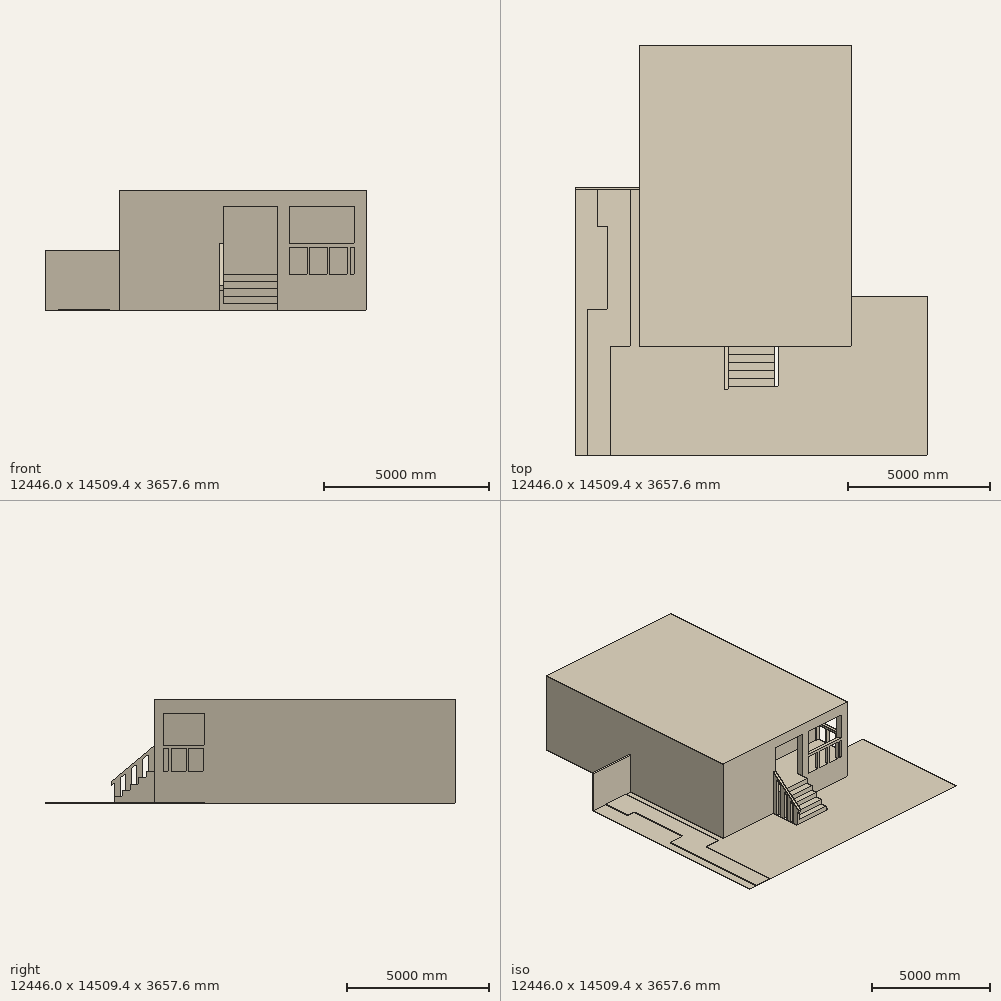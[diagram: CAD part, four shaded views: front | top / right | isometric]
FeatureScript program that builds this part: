
annotation { "Feature Type Name" : "Feature", "Feature Type Description" : "" }
export const myFeature = defineFeature(function(context is Context, id is Id, definition is map)
    precondition{}
    {
        {
            var Q0;
            Q0=qCreatedBy(makeId("Top.planeOp"),FACE);
            var sketch = newSketch(context, id + "F0", { "sketchPlane" : qUnion([Q0])});
            skLineSegment(sketch, "E0", {"start": v(0, 0) * mm, "end": v(0, 5562.6) * mm});
            skLineSegment(sketch, "E1", {"start": v(0, 5562.6) * mm, "end": v(-558.8, 5562.6) * mm});
            skLineSegment(sketch, "E2", {"start": v(-558.8, 5562.6) * mm, "end": v(-1498.6, 5562.6) * mm});
            skLineSegment(sketch, "E3", {"start": v(-1498.6, 5562.6) * mm, "end": v(-2260.6, 5562.6) * mm});
            skLineSegment(sketch, "E4", {"start": v(-2260.6, 5562.6) * mm, "end": v(-2260.6, -3860.8) * mm});
            skLineSegment(sketch, "E5", {"start": v(-2260.6, -3860.8) * mm, "end": v(10185.4, -3860.8) * mm});
            skLineSegment(sketch, "E6", {"start": v(10185.4, -3860.8) * mm, "end": v(10185.4, 0) * mm});
            skLineSegment(sketch, "E7", {"start": v(10185.4, 0) * mm, "end": v(10185.4, 2841.96) * mm});
            skLineSegment(sketch, "E8", {"start": v(10185.4, 2841.96) * mm, "end": v(10185.4, 6391.8) * mm});
            skLineSegment(sketch, "E9", {"start": v(10185.4, 6391.8) * mm, "end": v(7493, 6391.8) * mm});
            skLineSegment(sketch, "E10", {"start": v(7493, 6391.8) * mm, "end": v(7493, 1778) * mm});
            skLineSegment(sketch, "E11", {"start": v(7493, 1778) * mm, "end": v(7493, 0) * mm});
            skLineSegment(sketch, "E12", {"start": v(7493, 0) * mm, "end": v(4775.2, 0) * mm});
            skLineSegment(sketch, "E13", {"start": v(4775.2, 0) * mm, "end": v(4775.2, -1422.4) * mm});
            skLineSegment(sketch, "E14", {"start": v(4775.2, -1422.4) * mm, "end": v(4775.2, -3860.8) * mm});
            skLineSegment(sketch, "E15", {"start": v(0, 0) * mm, "end": v(3149.6, 0) * mm});
            skLineSegment(sketch, "E16", {"start": v(3149.6, 0) * mm, "end": v(3149.6, -1422.4) * mm});
            skLineSegment(sketch, "E17", {"start": v(3149.6, -1422.4) * mm, "end": v(2895.6, -1422.4) * mm});
            skLineSegment(sketch, "E18", {"start": v(2895.6, -1422.4) * mm, "end": v(2895.6, -3860.8) * mm});
            skLineSegment(sketch, "E19", {"start": v(-2134.8, -5689.6) * mm, "end": v(10320.05, -5689.6) * mm});
            skLineSegment(sketch, "E20", {"start": v(-2158.89, -6502.4) * mm, "end": v(10392.32, -6502.4) * mm});
            skSolve(sketch);
        }
        {
            var Q0;
            Q0=qCreatedBy(makeId("Top.planeOp"),FACE);
            var sketch = newSketch(context, id + "F1", { "sketchPlane" : qUnion([Q0])});
            skLineSegment(sketch, "E21.bottom", {"start": v(-1498.6, 5562.6) * mm, "end": v(-304.8, 5562.6) * mm});
            skLineSegment(sketch, "E22.left", {"start": v(-1117.6, 4241.8) * mm, "end": v(-1117.6, 1320.8) * mm});
            skLineSegment(sketch, "E22.right", {"start": v(-304.8, 4244.88) * mm, "end": v(-304.8, 0) * mm});
            skLineSegment(sketch, "E23.bottom", {"start": v(-1854.2, 1320.8) * mm, "end": v(-1117.6, 1320.8) * mm});
            skLineSegment(sketch, "E23.top", {"start": v(-1854.2, -3860.8) * mm, "end": v(-1041.4, -3860.8) * mm});
            skLineSegment(sketch, "E23.left", {"start": v(-1854.2, 1320.8) * mm, "end": v(-1854.2, -3860.8) * mm});
            skLineSegment(sketch, "E23.right", {"start": v(-1041.4, 0) * mm, "end": v(-1041.4, -3860.8) * mm});
            skLineSegment(sketch, "E24.top", {"start": v(-304.8, 0) * mm, "end": v(-1041.4, 0) * mm});
            skLineSegment(sketch, "E24.left", {"start": v(-304.8, 0) * mm, "end": v(-304.8, 0) * mm});
            skLineSegment(sketch, "E25", {"start": v(-304.8, 4244.88) * mm, "end": v(-304.8, 5562.6) * mm});
            skLineSegment(sketch, "E26", {"start": v(-1117.6, 4241.8) * mm, "end": v(-1498.6, 4241.8) * mm});
            skLineSegment(sketch, "E27", {"start": v(-1498.6, 4241.8) * mm, "end": v(-1498.6, 5562.6) * mm});
            skSolve(sketch);
        }
        {
            var Q0;
            Q0=qCreatedBy(makeId("Top.planeOp"),FACE);
            var sketch = newSketch(context, id + "F2", { "sketchPlane" : qUnion([Q0])});
            skLineSegment(sketch, "E28.bottom", {"start": v(0, 0) * mm, "end": v(7493, 0) * mm});
            skLineSegment(sketch, "E28.top", {"start": v(0, 10648.55) * mm, "end": v(7493, 10648.55) * mm});
            skLineSegment(sketch, "E28.left", {"start": v(0, 0) * mm, "end": v(0, 10648.55) * mm});
            skLineSegment(sketch, "E28.right", {"start": v(7493, 0) * mm, "end": v(7493, 10648.55) * mm});
            skSolve(sketch);
        }
        {
            var Q0;
            Q0 = qSketchRegion(id + "F2", true);
            extrude(context, id + "F3", {"entities" : qUnion([Q0]), "depth" : 3657.6 * mm, "offsetDistance" : 25.4 * mm});
        }
        {
            var Q0;
            Q0=makeQuery(id+"F3.opExtrude","SWEPT_FACE",FACE,{"disambiguationData":[OSD([sQuery(id+"F2.wireOp",EDGE,"E28.bottom")])]});
            var sketch = newSketch(context, id + "F4", { "sketchPlane" : qUnion([Q0])});
            skLineSegment(sketch, "E29.bottom", {"start": v(7493, 3167.33) * mm, "end": v(3149.6, 3167.33) * mm});
            skLineSegment(sketch, "E29.top", {"start": v(7493, 1114.2) * mm, "end": v(3149.6, 1114.2) * mm});
            skLineSegment(sketch, "E29.left", {"start": v(7493, 3167.33) * mm, "end": v(7493, 1114.2) * mm});
            skLineSegment(sketch, "E29.right", {"start": v(3149.6, 3167.33) * mm, "end": v(3149.6, 1114.2) * mm});
            skSolve(sketch);
        }
        {
            var Q0;
            Q0 = qSketchRegion(id + "F4", true);
            extrude(context, id + "F5", {"entities" : qUnion([Q0]), "operationType" : NewBodyOperationType.REMOVE, "oppositeDirection" : true, "depth" : 1778 * mm, "offsetDistance" : 25.4 * mm});
        }
        {
            var Q0;
            Q0=makeQuery(id+"F5.boolean.opBoolean","COPY",FACE,{"derivedFrom":makeQuery(id+"F5.opExtrude","SWEPT_FACE",FACE,{"disambiguationData":[OSD([sQuery(id+"F4.wireOp",EDGE,"E29.top")])]})});
            var sketch = newSketch(context, id + "F6", { "sketchPlane" : qUnion([Q0])});
            skLineSegment(sketch, "E30", {"start": v(4775.2, 0) * mm, "end": v(4775.2, 152.4) * mm});
            skLineSegment(sketch, "E31", {"start": v(4775.2, 152.4) * mm, "end": v(7340.6, 152.4) * mm});
            skLineSegment(sketch, "E32", {"start": v(7340.6, 152.4) * mm, "end": v(7340.6, 1778) * mm});
            skLineSegment(sketch, "E33", {"start": v(7340.6, 1778) * mm, "end": v(7493, 1778) * mm});
            skLineSegment(sketch, "E34", {"start": v(7493, 1778) * mm, "end": v(7493, 0) * mm});
            skLineSegment(sketch, "E35", {"start": v(7493, 0) * mm, "end": v(4775.2, 0) * mm});
            skSolve(sketch);
        }
        {
            var Q0;
            Q0=makeQuery(id+"F6.imprint","IMPRINT",FACE,{"disambiguationData":[TD([[makeQuery(id+"F6.imprint","IMPRINT",EDGE,{"derivedFrom":sQuery(id+"F6.wireOp",EDGE,"E30")}),-1.0]])]});
            extrude(context, id + "F7", {"entities" : qUnion([Q0]), "operationType" : NewBodyOperationType.ADD, "depth" : 914.4 * mm, "offsetDistance" : 25.4 * mm});
        }
        {
            var Q0;
            Q0=makeQuery(id+"F7.boolean.opBoolean","MERGE",FACE,{"derivedFrom":[makeQuery(id+"F3.opExtrude","SWEPT_FACE",FACE,{"disambiguationData":[OSD([sQuery(id+"F2.wireOp",EDGE,"E28.bottom")])]}),makeQuery(id+"F7.opExtrude","SWEPT_FACE",FACE,{"disambiguationData":[OSD([sQuery(id+"F6.wireOp",EDGE,"E35")])]})]});
            var sketch = newSketch(context, id + "F8", { "sketchPlane" : qUnion([Q0])});
            skLineSegment(sketch, "E36.bottom", {"start": v(5080, 1927) * mm, "end": v(5156.2, 1927) * mm, "construction": true});
            skLineSegment(sketch, "E36.top", {"start": v(5080, 1114.2) * mm, "end": v(5156.2, 1114.2) * mm, "construction": true});
            skLineSegment(sketch, "E36.left", {"start": v(5080, 1927) * mm, "end": v(5080, 1114.2) * mm, "construction": true});
            skLineSegment(sketch, "E36.right", {"start": v(5156.2, 1927) * mm, "end": v(5156.2, 1114.2) * mm, "construction": true});
            skLineSegment(sketch, "E37.1.0.0", {"start": v(5765.8, 1927) * mm, "end": v(5765.8, 1114.2) * mm, "construction": true});
            skLineSegment(sketch, "E37.1.0.1", {"start": v(5689.6, 1927) * mm, "end": v(5765.8, 1927) * mm, "construction": true});
            skLineSegment(sketch, "E37.1.0.2", {"start": v(5689.6, 1927) * mm, "end": v(5689.6, 1114.2) * mm, "construction": true});
            skLineSegment(sketch, "E37.1.0.3", {"start": v(5689.6, 1114.2) * mm, "end": v(5765.8, 1114.2) * mm, "construction": true});
            skLineSegment(sketch, "E37.2.0.0", {"start": v(6375.4, 1927) * mm, "end": v(6375.4, 1114.2) * mm, "construction": true});
            skLineSegment(sketch, "E37.2.0.1", {"start": v(6299.2, 1927) * mm, "end": v(6375.4, 1927) * mm, "construction": true});
            skLineSegment(sketch, "E37.2.0.2", {"start": v(6299.2, 1927) * mm, "end": v(6299.2, 1114.2) * mm, "construction": true});
            skLineSegment(sketch, "E37.2.0.3", {"start": v(6299.2, 1114.2) * mm, "end": v(6375.4, 1114.2) * mm, "construction": true});
            skLineSegment(sketch, "E37.3.0.0", {"start": v(6985, 1927) * mm, "end": v(6985, 1114.2) * mm, "construction": true});
            skLineSegment(sketch, "E37.3.0.1", {"start": v(6908.8, 1927) * mm, "end": v(6985, 1927) * mm, "construction": true});
            skLineSegment(sketch, "E37.3.0.2", {"start": v(6908.8, 1927) * mm, "end": v(6908.8, 1114.2) * mm, "construction": true});
            skLineSegment(sketch, "E37.3.0.3", {"start": v(6908.8, 1114.2) * mm, "end": v(6985, 1114.2) * mm, "construction": true});
            skLineSegment(sketch, "E37.direction1", {"start": v(5156.2, 1114.2) * mm, "end": v(5765.8, 1114.2) * mm, "construction": true});
            skLineSegment(sketch, "E38.bottom", {"start": v(5156.2, 1927) * mm, "end": v(5689.6, 1927) * mm, "construction": true});
            skLineSegment(sketch, "E38.top", {"start": v(5156.2, 1114.2) * mm, "end": v(5689.6, 1114.2) * mm, "construction": true});
            skLineSegment(sketch, "E39.bottom", {"start": v(5765.8, 1114.2) * mm, "end": v(6299.2, 1114.2) * mm, "construction": true});
            skLineSegment(sketch, "E39.top", {"start": v(5765.8, 1927) * mm, "end": v(6299.2, 1927) * mm, "construction": true});
            skLineSegment(sketch, "E39.left", {"start": v(5765.8, 1114.2) * mm, "end": v(5765.8, 1927) * mm, "construction": true});
            skLineSegment(sketch, "E39.right", {"start": v(6299.2, 1114.2) * mm, "end": v(6299.2, 1927) * mm, "construction": true});
            skLineSegment(sketch, "E40.bottom", {"start": v(6375.4, 1927) * mm, "end": v(6908.8, 1927) * mm, "construction": true});
            skLineSegment(sketch, "E40.top", {"start": v(6375.4, 1114.2) * mm, "end": v(6908.8, 1114.2) * mm, "construction": true});
            skLineSegment(sketch, "E41.bottom", {"start": v(5156.2, 1927) * mm, "end": v(5689.6, 1927) * mm});
            skLineSegment(sketch, "E41.top", {"start": v(5156.2, 1114.2) * mm, "end": v(5689.6, 1114.2) * mm});
            skLineSegment(sketch, "E41.left", {"start": v(5156.2, 1927) * mm, "end": v(5156.2, 1114.2) * mm});
            skLineSegment(sketch, "E41.right", {"start": v(5689.6, 1927) * mm, "end": v(5689.6, 1114.2) * mm});
            skLineSegment(sketch, "E42.bottom", {"start": v(5765.8, 1114.2) * mm, "end": v(6299.2, 1114.2) * mm});
            skLineSegment(sketch, "E42.top", {"start": v(5765.8, 1927) * mm, "end": v(6299.2, 1927) * mm});
            skLineSegment(sketch, "E42.left", {"start": v(5765.8, 1114.2) * mm, "end": v(5765.8, 1927) * mm});
            skLineSegment(sketch, "E42.right", {"start": v(6299.2, 1114.2) * mm, "end": v(6299.2, 1927) * mm});
            skLineSegment(sketch, "E43.bottom", {"start": v(6375.4, 1927) * mm, "end": v(6908.8, 1927) * mm});
            skLineSegment(sketch, "E43.top", {"start": v(6375.4, 1114.2) * mm, "end": v(6908.8, 1114.2) * mm});
            skLineSegment(sketch, "E43.left", {"start": v(6375.4, 1927) * mm, "end": v(6375.4, 1114.2) * mm});
            skLineSegment(sketch, "E43.right", {"start": v(6908.8, 1927) * mm, "end": v(6908.8, 1114.2) * mm});
            skSolve(sketch);
        }
        {
            var Q0;
            Q0 = qSketchRegion(id + "F8", true);
            extrude(context, id + "F9", {"entities" : qUnion([Q0]), "operationType" : NewBodyOperationType.REMOVE, "oppositeDirection" : true, "depth" : 304.8 * mm, "offsetDistance" : 25.4 * mm});
        }
        {
            var Q0;
            Q0=makeQuery(id+"F7.boolean.opBoolean","MERGE",FACE,{"derivedFrom":[makeQuery(id+"F3.opExtrude","SWEPT_FACE",FACE,{"disambiguationData":[OSD([sQuery(id+"F2.wireOp",EDGE,"E28.right")])]}),makeQuery(id+"F7.opExtrude","SWEPT_FACE",FACE,{"disambiguationData":[OSD([sQuery(id+"F6.wireOp",EDGE,"E34")])]})]});
            var sketch = newSketch(context, id + "F10", { "sketchPlane" : qUnion([Q0])});
            skLineSegment(sketch, "E44.bottom", {"start": v(1727.2, 1927) * mm, "end": v(1193.8, 1927) * mm});
            skLineSegment(sketch, "E44.top", {"start": v(1727.2, 1114.2) * mm, "end": v(1193.8, 1114.2) * mm});
            skLineSegment(sketch, "E44.left", {"start": v(1727.2, 1927) * mm, "end": v(1727.2, 1114.2) * mm});
            skLineSegment(sketch, "E44.right", {"start": v(1193.8, 1927) * mm, "end": v(1193.8, 1114.2) * mm});
            skLineSegment(sketch, "E45.bottom", {"start": v(1117.6, 1927) * mm, "end": v(584.2, 1927) * mm});
            skLineSegment(sketch, "E45.top", {"start": v(1117.6, 1114.2) * mm, "end": v(584.2, 1114.2) * mm});
            skLineSegment(sketch, "E45.left", {"start": v(1117.6, 1927) * mm, "end": v(1117.6, 1114.2) * mm});
            skLineSegment(sketch, "E45.right", {"start": v(584.2, 1927) * mm, "end": v(584.2, 1114.2) * mm});
            skSolve(sketch);
        }
        {
            var Q0;
            Q0 = qSketchRegion(id + "F10", true);
            extrude(context, id + "F11", {"entities" : qUnion([Q0]), "operationType" : NewBodyOperationType.REMOVE, "oppositeDirection" : true, "depth" : 254 * mm, "offsetDistance" : 25.4 * mm});
        }
        {
            var Q0;
            Q0=makeQuery(id+"F11.boolean.opBoolean","MERGE",FACE,{"derivedFrom":[makeQuery(id+"F9.boolean.opBoolean","MERGE",FACE,{"derivedFrom":[makeQuery(id+"F5.boolean.opBoolean","COPY",FACE,{"derivedFrom":makeQuery(id+"F5.opExtrude","SWEPT_FACE",FACE,{"disambiguationData":[OSD([sQuery(id+"F4.wireOp",EDGE,"E29.top")])]})}),makeQuery(id+"F9.opExtrude","SWEPT_FACE",FACE,{"disambiguationData":[OSD([sQuery(id+"F8.wireOp",EDGE,"E41.top")])]}),makeQuery(id+"F9.opExtrude","SWEPT_FACE",FACE,{"disambiguationData":[OSD([sQuery(id+"F8.wireOp",EDGE,"E42.bottom")])]}),makeQuery(id+"F9.opExtrude","SWEPT_FACE",FACE,{"disambiguationData":[OSD([sQuery(id+"F8.wireOp",EDGE,"E43.top")])]})]}),makeQuery(id+"F11.opExtrude","SWEPT_FACE",FACE,{"disambiguationData":[OSD([sQuery(id+"F10.wireOp",EDGE,"E44.top")])]}),makeQuery(id+"F11.opExtrude","SWEPT_FACE",FACE,{"disambiguationData":[OSD([sQuery(id+"F10.wireOp",EDGE,"E45.top")])]})]});
            var sketch = newSketch(context, id + "F12", { "sketchPlane" : qUnion([Q0])});
            skLineSegment(sketch, "E46.bottom", {"start": v(4775.2, 0) * mm, "end": v(5156.2, 0) * mm});
            skLineSegment(sketch, "E46.top", {"start": v(4775.2, 304.8) * mm, "end": v(5156.2, 304.8) * mm});
            skLineSegment(sketch, "E46.left", {"start": v(4775.2, 0) * mm, "end": v(4775.2, 304.8) * mm});
            skLineSegment(sketch, "E46.right", {"start": v(5156.2, 0) * mm, "end": v(5156.2, 304.8) * mm});
            skLineSegment(sketch, "E47.bottom", {"start": v(7112, 304.8) * mm, "end": v(7493, 304.8) * mm});
            skLineSegment(sketch, "E47.top", {"start": v(7112, 0) * mm, "end": v(7493, 0) * mm});
            skLineSegment(sketch, "E47.left", {"start": v(7112, 304.8) * mm, "end": v(7112, 0) * mm});
            skLineSegment(sketch, "E47.right", {"start": v(7493, 304.8) * mm, "end": v(7493, 0) * mm});
            skSolve(sketch);
        }
        {
            var Q0;
            Q0 = qSketchRegion(id + "F12", true);
            extrude(context, id + "F13", {"entities" : qUnion([Q0]), "operationType" : NewBodyOperationType.ADD, "depth" : 2540 * mm, "offsetDistance" : 25.4 * mm});
        }
        {
            var Q0;
            Q0=makeQuery(id+"F13.boolean.opBoolean","MERGE",FACE,{"derivedFrom":[makeQuery(id+"F7.boolean.opBoolean","MERGE",FACE,{"derivedFrom":[makeQuery(id+"F3.opExtrude","SWEPT_FACE",FACE,{"disambiguationData":[OSD([sQuery(id+"F2.wireOp",EDGE,"E28.right")])]}),makeQuery(id+"F7.opExtrude","SWEPT_FACE",FACE,{"disambiguationData":[OSD([sQuery(id+"F6.wireOp",EDGE,"E34")])]})]}),makeQuery(id+"F13.opExtrude","SWEPT_FACE",FACE,{"disambiguationData":[OSD([sQuery(id+"F12.wireOp",EDGE,"E47.right")])]})]});
            var sketch = newSketch(context, id + "F14", { "sketchPlane" : qUnion([Q0])});
            skLineSegment(sketch, "E48.bottom", {"start": v(508, 1927) * mm, "end": v(304.8, 1927) * mm});
            skLineSegment(sketch, "E48.top", {"start": v(508, 1114.2) * mm, "end": v(304.8, 1114.2) * mm});
            skLineSegment(sketch, "E48.left", {"start": v(508, 1927) * mm, "end": v(508, 1114.2) * mm});
            skLineSegment(sketch, "E48.right", {"start": v(304.8, 1927) * mm, "end": v(304.8, 1114.2) * mm});
            skSolve(sketch);
        }
        {
            var Q0;
            Q0 = qSketchRegion(id + "F14", true);
            extrude(context, id + "F15", {"entities" : qUnion([Q0]), "operationType" : NewBodyOperationType.REMOVE, "oppositeDirection" : true, "depth" : 254 * mm, "offsetDistance" : 25.4 * mm});
        }
        {
            var Q0;
            Q0=makeQuery(id+"F13.boolean.opBoolean","MERGE",FACE,{"derivedFrom":[makeQuery(id+"F7.boolean.opBoolean","MERGE",FACE,{"derivedFrom":[makeQuery(id+"F3.opExtrude","SWEPT_FACE",FACE,{"disambiguationData":[OSD([sQuery(id+"F2.wireOp",EDGE,"E28.bottom")])]}),makeQuery(id+"F7.opExtrude","SWEPT_FACE",FACE,{"disambiguationData":[OSD([sQuery(id+"F6.wireOp",EDGE,"E35")])]})]}),makeQuery(id+"F13.opExtrude","SWEPT_FACE",FACE,{"disambiguationData":[OSD([sQuery(id+"F12.wireOp",EDGE,"E46.bottom")])]}),makeQuery(id+"F13.opExtrude","SWEPT_FACE",FACE,{"disambiguationData":[OSD([sQuery(id+"F12.wireOp",EDGE,"E47.top")])]})]});
            var sketch = newSketch(context, id + "F16", { "sketchPlane" : qUnion([Q0])});
            skLineSegment(sketch, "E49.bottom", {"start": v(6985, 1927) * mm, "end": v(7112, 1927) * mm});
            skLineSegment(sketch, "E49.top", {"start": v(6985, 1114.2) * mm, "end": v(7112, 1114.2) * mm});
            skLineSegment(sketch, "E49.left", {"start": v(6985, 1927) * mm, "end": v(6985, 1114.2) * mm});
            skLineSegment(sketch, "E49.right", {"start": v(7112, 1927) * mm, "end": v(7112, 1114.2) * mm});
            skSolve(sketch);
        }
        {
            var Q0;
            Q0=makeQuery(id+"F5.boolean.opBoolean","COPY",FACE,{"derivedFrom":makeQuery(id+"F5.opExtrude","SWEPT_FACE",FACE,{"disambiguationData":[OSD([sQuery(id+"F4.wireOp",EDGE,"E29.right")])]})});
            cPlane(context, id + "F17", {"entities" : qUnion([Q0]), "cplaneType" : CPlaneType.OFFSET, "offset" : 0 * mm, "width" : 152.4 * mm, "height" : 152.4 * mm});
        }
        {
            var Q0;
            Q0 = qSketchRegion(id + "F16", true);
            extrude(context, id + "F18", {"entities" : qUnion([Q0]), "operationType" : NewBodyOperationType.REMOVE, "oppositeDirection" : true, "depth" : 254 * mm, "offsetDistance" : 25.4 * mm});
        }
        {
            var Q0;
            Q0=qCreatedBy(id+"F17.planeOp",FACE);
            var sketch = newSketch(context, id + "F19", { "sketchPlane" : qUnion([Q0])});
            skLineSegment(sketch, "E50", {"start": v(0, 1114.2) * mm, "end": v(-284.48, 1114.2) * mm});
            skLineSegment(sketch, "E51", {"start": v(-284.48, 891.36) * mm, "end": v(-568.96, 891.36) * mm});
            skLineSegment(sketch, "E52", {"start": v(-568.96, 891.36) * mm, "end": v(-568.96, 668.52) * mm});
            skLineSegment(sketch, "E53", {"start": v(-568.96, 668.52) * mm, "end": v(-853.44, 668.52) * mm});
            skLineSegment(sketch, "E54", {"start": v(-853.44, 668.52) * mm, "end": v(-853.44, 445.68) * mm});
            skLineSegment(sketch, "E55", {"start": v(-1422.4, 222.84) * mm, "end": v(-1422.4, 0) * mm});
            skLineSegment(sketch, "E56", {"start": v(-1422.4, 0) * mm, "end": v(0, 0) * mm});
            skLineSegment(sketch, "E57", {"start": v(0, 0) * mm, "end": v(0, 1114.2) * mm});
            skLineSegment(sketch, "E58", {"start": v(-1422.4, 222.84) * mm, "end": v(-1137.92, 222.84) * mm});
            skLineSegment(sketch, "E59", {"start": v(-1137.92, 222.84) * mm, "end": v(-1137.92, 445.68) * mm});
            skLineSegment(sketch, "E60", {"start": v(-1137.92, 445.68) * mm, "end": v(-853.44, 445.68) * mm});
            skLineSegment(sketch, "E61", {"start": v(-284.48, 891.36) * mm, "end": v(-284.48, 1114.2) * mm});
            skSolve(sketch);
        }
        {
            var Q0;
            Q0 = qSketchRegion(id + "F19", true);
            var Q1;
            Q1=makeQuery(id+"F13.boolean.opBoolean","MERGE",FACE,{"derivedFrom":[makeQuery(id+"F7.opExtrude","SWEPT_FACE",FACE,{"disambiguationData":[OSD([sQuery(id+"F6.wireOp",EDGE,"E30")])]}),makeQuery(id+"F13.opExtrude","SWEPT_FACE",FACE,{"disambiguationData":[OSD([sQuery(id+"F12.wireOp",EDGE,"E46.left")])]})]});
            extrude(context, id + "F20", {"entities" : qUnion([Q0]), "operationType" : NewBodyOperationType.ADD, "endBound" : BoundingType.UP_TO_SURFACE, "depth" : 25.4 * mm, "endBoundEntityFace" : qUnion([Q1]), "offsetDistance" : 25.4 * mm});
        }
        {
            var Q0;
            Q0=makeQuery(id+"F20.opExtrude","CAP_FACE",FACE,{"disambiguationData":[OSD([sQuery(id+"F19.wireOp",EDGE,"E50"),sQuery(id+"F19.wireOp",EDGE,"E51"),sQuery(id+"F19.wireOp",EDGE,"E52"),sQuery(id+"F19.wireOp",EDGE,"E53"),sQuery(id+"F19.wireOp",EDGE,"E54"),sQuery(id+"F19.wireOp",EDGE,"E55"),sQuery(id+"F19.wireOp",EDGE,"E56"),sQuery(id+"F19.wireOp",EDGE,"E57"),sQuery(id+"F19.wireOp",EDGE,"E58"),sQuery(id+"F19.wireOp",EDGE,"E59"),sQuery(id+"F19.wireOp",EDGE,"E60"),sQuery(id+"F19.wireOp",EDGE,"E61")])],"isStart":true});
            var sketch = newSketch(context, id + "F21", { "sketchPlane" : qUnion([Q0])});
            skLineSegment(sketch, "E62", {"start": v(0, 2030.33) * mm, "end": v(1524, 751.55) * mm});
            skLineSegment(sketch, "E63", {"start": v(1524, 751.55) * mm, "end": v(1524, 618.92) * mm});
            skLineSegment(sketch, "E64", {"start": v(1524, 618.92) * mm, "end": v(1422.4, 704.17) * mm});
            skLineSegment(sketch, "E65", {"start": v(1422.4, 704.17) * mm, "end": v(1422.4, 0) * mm});
            skLineSegment(sketch, "E66", {"start": v(1422.4, 0) * mm, "end": v(1219.2, 0) * mm});
            skLineSegment(sketch, "E67", {"start": v(1219.2, 0) * mm, "end": v(1219.2, 874.67) * mm});
            skLineSegment(sketch, "E68", {"start": v(1219.2, 874.67) * mm, "end": v(1033.67, 1030.35) * mm});
            skLineSegment(sketch, "E69", {"start": v(1033.67, 1030.35) * mm, "end": v(1033.67, 0) * mm});
            skLineSegment(sketch, "E70", {"start": v(1033.67, 0) * mm, "end": v(830.47, 0) * mm});
            skLineSegment(sketch, "E71", {"start": v(830.47, 0) * mm, "end": v(830.47, 1200.86) * mm});
            skLineSegment(sketch, "E72", {"start": v(830.47, 1200.86) * mm, "end": v(644.94, 1356.54) * mm});
            skLineSegment(sketch, "E73", {"start": v(644.94, 1356.54) * mm, "end": v(644.94, 0) * mm});
            skLineSegment(sketch, "E74", {"start": v(644.94, 0) * mm, "end": v(441.74, 0) * mm});
            skLineSegment(sketch, "E75", {"start": v(441.74, 0) * mm, "end": v(441.74, 1527.05) * mm});
            skLineSegment(sketch, "E76", {"start": v(441.74, 1527.05) * mm, "end": v(203.2, 1727.2) * mm});
            skLineSegment(sketch, "E77", {"start": v(203.2, 1727.2) * mm, "end": v(203.2, 0) * mm});
            skLineSegment(sketch, "E78", {"start": v(203.2, 0) * mm, "end": v(0, 0) * mm});
            skLineSegment(sketch, "E79", {"start": v(0, 0) * mm, "end": v(0, 2030.33) * mm});
            skSolve(sketch);
        }
        {
            var Q0;
            Q0 = qSketchRegion(id + "F21", true);
            extrude(context, id + "F22", {"entities" : qUnion([Q0]), "operationType" : NewBodyOperationType.ADD, "depth" : 127 * mm, "offsetDistance" : 25.4 * mm});
        }
        {
            var Q0;
            Q0=makeQuery(id+"F22.boolean.opBoolean","MERGE",FACE,{"derivedFrom":[makeQuery(id+"F5.boolean.opBoolean","COPY",FACE,{"derivedFrom":makeQuery(id+"F5.opExtrude","SWEPT_FACE",FACE,{"disambiguationData":[OSD([sQuery(id+"F4.wireOp",EDGE,"E29.right")])]})}),makeQuery(id+"F22.opExtrude","CAP_FACE",FACE,{"disambiguationData":[OSD([sQuery(id+"F21.wireOp",EDGE,"E62"),sQuery(id+"F21.wireOp",EDGE,"E63"),sQuery(id+"F21.wireOp",EDGE,"E64"),sQuery(id+"F21.wireOp",EDGE,"E65"),sQuery(id+"F21.wireOp",EDGE,"E66"),sQuery(id+"F21.wireOp",EDGE,"E67"),sQuery(id+"F21.wireOp",EDGE,"E68"),sQuery(id+"F21.wireOp",EDGE,"E69"),sQuery(id+"F21.wireOp",EDGE,"E70"),sQuery(id+"F21.wireOp",EDGE,"E71"),sQuery(id+"F21.wireOp",EDGE,"E72"),sQuery(id+"F21.wireOp",EDGE,"E73"),sQuery(id+"F21.wireOp",EDGE,"E74"),sQuery(id+"F21.wireOp",EDGE,"E75"),sQuery(id+"F21.wireOp",EDGE,"E76"),sQuery(id+"F21.wireOp",EDGE,"E77"),sQuery(id+"F21.wireOp",EDGE,"E78"),sQuery(id+"F21.wireOp",EDGE,"E79")])],"isStart":true})]});
            var Q1;
            Q1=makeQuery(id+"F13.boolean.opBoolean","MERGE",FACE,{"derivedFrom":[makeQuery(id+"F7.opExtrude","SWEPT_FACE",FACE,{"disambiguationData":[OSD([sQuery(id+"F6.wireOp",EDGE,"E30")])]}),makeQuery(id+"F13.opExtrude","SWEPT_FACE",FACE,{"disambiguationData":[OSD([sQuery(id+"F12.wireOp",EDGE,"E46.left")])]})]});
            cPlane(context, id + "F23", {"entities" : qUnion([Q0, Q1]), "cplaneType" : CPlaneType.MID_PLANE, "offset" : 25.4 * mm, "width" : 152.4 * mm, "height" : 152.4 * mm});
        }
        {
            var Q0;
            Q0=makeQuery(id+"F3.opExtrude","SWEPT_FACE",FACE,{"disambiguationData":[OSD([sQuery(id+"F2.wireOp",EDGE,"E28.left")])]});
            var sketch = newSketch(context, id + "F24", { "sketchPlane" : qUnion([Q0])});
            skLineSegment(sketch, "E80.bottom", {"start": v(-5638.8, 0) * mm, "end": v(-5562.6, 0) * mm});
            skLineSegment(sketch, "E80.top", {"start": v(-5638.8, 1828.8) * mm, "end": v(-5562.6, 1828.8) * mm});
            skLineSegment(sketch, "E80.left", {"start": v(-5638.8, 0) * mm, "end": v(-5638.8, 1828.8) * mm});
            skLineSegment(sketch, "E80.right", {"start": v(-5562.6, 0) * mm, "end": v(-5562.6, 1828.8) * mm});
            skSolve(sketch);
        }
        {
            var Q0;
            Q0 = qSketchRegion(id + "F24", true);
            var Q1;
            Q1=sQuery(id+"F0.wireOp",VERTEX,"E4.start");
            extrude(context, id + "F25", {"entities" : qUnion([Q0]), "operationType" : NewBodyOperationType.ADD, "endBound" : BoundingType.UP_TO_VERTEX, "depth" : 25.4 * mm, "endBoundEntityVertex" : qUnion([Q1]), "offsetDistance" : 25.4 * mm});
        }
        {
            var Q0;
            Q0=makeQuery(id+"F1.imprint","IMPRINT",FACE,{"disambiguationData":[TD([[makeQuery(id+"F1.imprint","IMPRINT",EDGE,{"derivedFrom":sQuery(id+"F1.wireOp",EDGE,"E21.bottom")}),-1.0]])]});
            extrude(context, id + "F26", {"entities" : qUnion([Q0]), "operationType" : NewBodyOperationType.ADD, "depth" : 25.4 * mm, "offsetDistance" : 25.4 * mm});
        }
        {
            var Q0;
            Q0=qCreatedBy(makeId("Top.planeOp"),FACE);
            var sketch = newSketch(context, id + "F27", { "sketchPlane" : qUnion([Q0])});
            skLineSegment(sketch, "E81.bottom", {"start": v(-2260.6, 5562.6) * mm, "end": v(0, 5562.6) * mm});
            skLineSegment(sketch, "E81.top", {"start": v(-2260.6, -3860.8) * mm, "end": v(0, -3860.8) * mm});
            skLineSegment(sketch, "E81.left", {"start": v(-2260.6, 5562.6) * mm, "end": v(-2260.6, -3860.8) * mm});
            skLineSegment(sketch, "E81.right", {"start": v(0, 5562.6) * mm, "end": v(0, 0) * mm});
            skLineSegment(sketch, "E82", {"start": v(0, 0) * mm, "end": v(3022.6, 0) * mm});
            skLineSegment(sketch, "E83", {"start": v(3022.6, 0) * mm, "end": v(3022.6, -1422.4) * mm});
            skLineSegment(sketch, "E84", {"start": v(3022.6, -1422.4) * mm, "end": v(4775.2, -1422.4) * mm});
            skLineSegment(sketch, "E85", {"start": v(4902.2, -1422.4) * mm, "end": v(4902.2, 0) * mm});
            skLineSegment(sketch, "E86", {"start": v(4902.2, 0) * mm, "end": v(7493, 0) * mm});
            skLineSegment(sketch, "E87", {"start": v(7493, 0) * mm, "end": v(7493, 1778) * mm});
            skLineSegment(sketch, "E88", {"start": v(7493, 1778) * mm, "end": v(10185.4, 1778) * mm});
            skLineSegment(sketch, "E89", {"start": v(10185.4, 1778) * mm, "end": v(10185.4, -3860.8) * mm});
            skLineSegment(sketch, "E90", {"start": v(10185.4, -3860.8) * mm, "end": v(0, -3860.8) * mm});
            skLineSegment(sketch, "E91", {"start": v(4775.2, -1422.4) * mm, "end": v(4902.2, -1422.4) * mm});
            skPoint(sketch, "E92.orphan", {"position": v(4963.02, -1422.4) * mm});
            skSolve(sketch);
        }
        {
            var Q0;
            Q0 = qSketchRegion(id + "F27", true);
            extrude(context, id + "F28", {"entities" : qUnion([Q0]), "operationType" : NewBodyOperationType.ADD, "depth" : 6.35 * mm, "offsetDistance" : 25.4 * mm});
        }
    });
